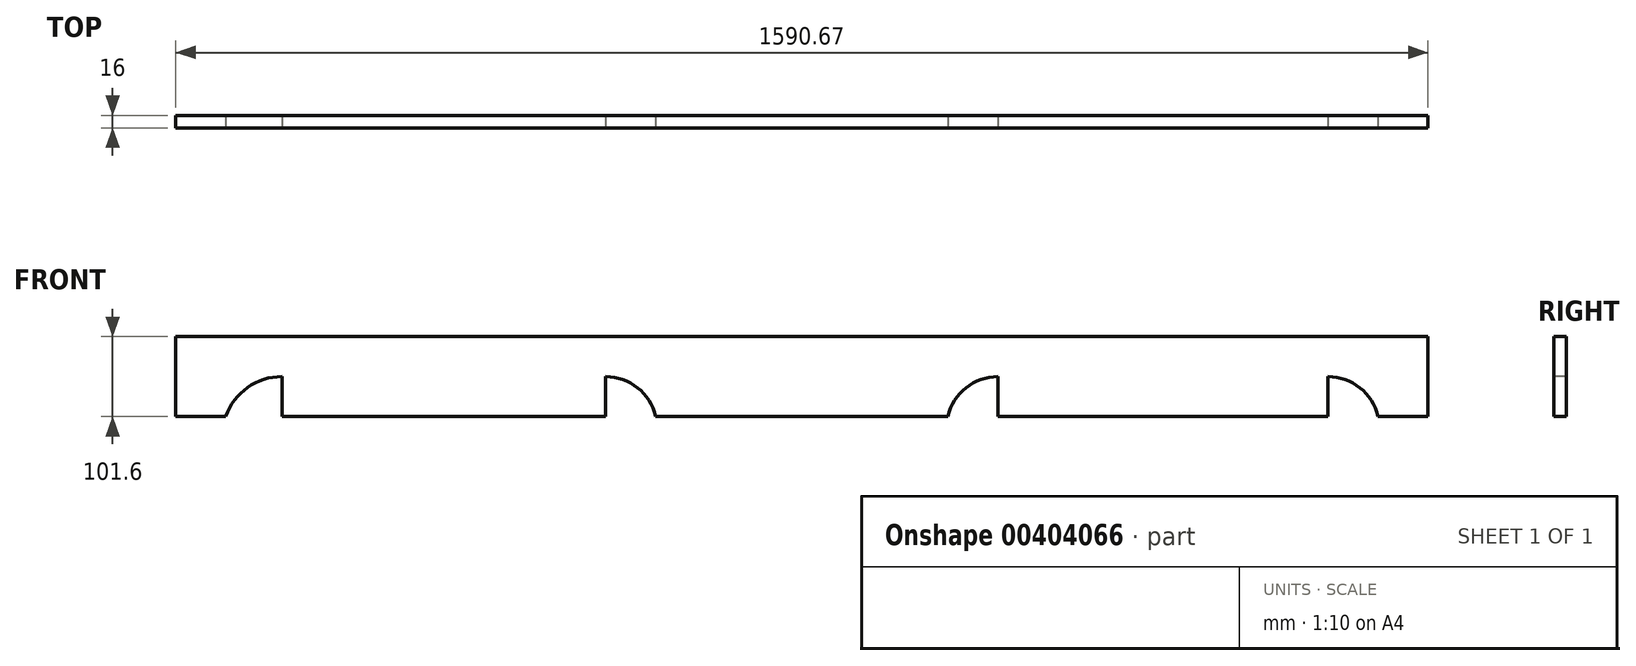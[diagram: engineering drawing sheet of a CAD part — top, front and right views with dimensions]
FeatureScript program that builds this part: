
annotation { "Feature Type Name" : "Feature", "Feature Type Description" : "" }
export const myFeature = defineFeature(function(context is Context, id is Id, definition is map)
    precondition{}
    {
        {
            var Q0;
            Q0=qCreatedBy(makeId("Front.planeOp"),FACE);
            var sketch = newSketch(context, id + "F0", { "sketchPlane" : qUnion([Q0])});
            skLineSegment(sketch, "E0.bottom", {"start": v(-777.17, 28) * mm, "end": v(813.5, 28) * mm});
            skLineSegment(sketch, "E0.top", {"start": v(-777.17, -73.6) * mm, "end": v(813.5, -73.6) * mm});
            skLineSegment(sketch, "E0.left", {"start": v(-777.17, 28) * mm, "end": v(-777.17, -73.6) * mm});
            skLineSegment(sketch, "E0.right", {"start": v(813.5, 28) * mm, "end": v(813.5, -73.6) * mm});
            skSolve(sketch);
        }
        {
            var Q0;
            Q0 = qSketchRegion(id + "F0", true);
            extrude(context, id + "F1", {"entities" : qUnion([Q0]), "depth" : 16 * mm});
        }
        {
            var Q0;
            Q0=makeQuery(id+"F1.opExtrude","CAP_FACE",FACE,{"disambiguationData":[OSD([sQuery(id+"F0.wireOp",EDGE,"E0.bottom"),sQuery(id+"F0.wireOp",EDGE,"E0.top"),sQuery(id+"F0.wireOp",EDGE,"E0.left"),sQuery(id+"F0.wireOp",EDGE,"E0.right")])],"isStart":false});
            var sketch = newSketch(context, id + "F2", { "sketchPlane" : qUnion([Q0])});
            skLineSegment(sketch, "E1.bottom", {"start": v(-167.57, 28) * mm, "end": v(203.9, 28) * mm});
            skLineSegment(sketch, "E1.top", {"start": v(-167.57, -73.6) * mm, "end": v(203.9, -73.6) * mm});
            skLineSegment(sketch, "E1.left", {"start": v(-167.57, 28) * mm, "end": v(-167.57, -73.6) * mm});
            skLineSegment(sketch, "E1.right", {"start": v(203.9, 28) * mm, "end": v(203.9, -73.6) * mm});
            skLineSegment(sketch, "E2.bottom", {"start": v(-777.17, -73.6) * mm, "end": v(-167.57, -73.6) * mm});
            skLineSegment(sketch, "E2.top", {"start": v(-777.17, -22.8) * mm, "end": v(-167.57, -22.8) * mm});
            skLineSegment(sketch, "E2.left", {"start": v(-777.17, -73.6) * mm, "end": v(-777.17, -22.8) * mm});
            skLineSegment(sketch, "E2.right", {"start": v(-167.57, -73.6) * mm, "end": v(-167.57, -22.8) * mm});
            skLineSegment(sketch, "E3.bottom", {"start": v(203.9, -73.6) * mm, "end": v(813.5, -73.6) * mm});
            skLineSegment(sketch, "E3.top", {"start": v(203.9, -22.8) * mm, "end": v(813.5, -22.8) * mm});
            skLineSegment(sketch, "E3.left", {"start": v(203.9, -73.6) * mm, "end": v(203.9, -22.8) * mm});
            skLineSegment(sketch, "E3.right", {"start": v(813.5, -73.6) * mm, "end": v(813.5, -22.8) * mm});
            skLineSegment(sketch, "E4.bottom", {"start": v(-777.17, -22.8) * mm, "end": v(-713.67, -22.8) * mm});
            skLineSegment(sketch, "E4.top", {"start": v(-777.17, -73.6) * mm, "end": v(-713.67, -73.6) * mm});
            skLineSegment(sketch, "E4.left", {"start": v(-777.17, -22.8) * mm, "end": v(-777.17, -73.6) * mm});
            skLineSegment(sketch, "E4.right", {"start": v(-713.67, -22.8) * mm, "end": v(-713.67, -73.6) * mm});
            skLineSegment(sketch, "E5.bottom", {"start": v(-167.57, -73.6) * mm, "end": v(-231.07, -73.6) * mm});
            skLineSegment(sketch, "E5.top", {"start": v(-167.57, -22.8) * mm, "end": v(-231.07, -22.8) * mm});
            skLineSegment(sketch, "E5.right", {"start": v(-231.07, -73.6) * mm, "end": v(-231.07, -22.8) * mm});
            skLineSegment(sketch, "E6.bottom", {"start": v(203.9, -73.6) * mm, "end": v(267.4, -73.6) * mm});
            skLineSegment(sketch, "E6.top", {"start": v(203.9, -22.8) * mm, "end": v(267.4, -22.8) * mm});
            skLineSegment(sketch, "E6.right", {"start": v(267.4, -73.6) * mm, "end": v(267.4, -22.8) * mm});
            skLineSegment(sketch, "E7.bottom", {"start": v(813.5, -73.6) * mm, "end": v(750, -73.6) * mm});
            skLineSegment(sketch, "E7.top", {"start": v(813.5, -22.8) * mm, "end": v(750, -22.8) * mm});
            skLineSegment(sketch, "E7.right", {"start": v(750, -73.6) * mm, "end": v(750, -22.8) * mm});
            skLineSegment(sketch, "E8.bottom", {"start": v(-713.67, -22.8) * mm, "end": v(-642.03, -22.8) * mm});
            skLineSegment(sketch, "E8.top", {"start": v(-713.67, -73.6) * mm, "end": v(-642.03, -73.6) * mm});
            skLineSegment(sketch, "E8.right", {"start": v(-642.03, -22.8) * mm, "end": v(-642.03, -73.6) * mm});
            skLineSegment(sketch, "E9.bottom", {"start": v(750, -73.6) * mm, "end": v(686.5, -73.6) * mm});
            skLineSegment(sketch, "E9.top", {"start": v(750, -22.8) * mm, "end": v(686.5, -22.8) * mm});
            skLineSegment(sketch, "E9.right", {"start": v(686.5, -73.6) * mm, "end": v(686.5, -22.8) * mm});
            skArc(sketch, "E10", {"start": v(267.4, -22.8) * mm, "mid": v(226.74, -37.07) * mm, "end": v(203.9, -73.6) * mm});
            skArc(sketch, "E11", {"start": v(750, -73.6) * mm, "mid": v(727.16, -37.07) * mm, "end": v(686.5, -22.8) * mm});
            skArc(sketch, "E12", {"start": v(-642.03, -22.8) * mm, "mid": v(-685.95, -36.8) * mm, "end": v(-713.67, -73.6) * mm});
            skArc(sketch, "E13", {"start": v(-167.57, -73.6) * mm, "mid": v(-190.41, -37.07) * mm, "end": v(-231.07, -22.8) * mm});
            skSolve(sketch);
        }
        {
            var Q0;
            Q0=makeQuery(id+"F2.imprint","IMPRINT",FACE,{"disambiguationData":[TD([[makeQuery(id+"F2.imprint","IMPRINT",EDGE,{"derivedFrom":sQuery(id+"F2.wireOp",EDGE,"E8.top")}),1.0]])]});
            var Q1;
            Q1=makeQuery(id+"F2.imprint","IMPRINT",FACE,{"disambiguationData":[TD([[makeQuery(id+"F2.imprint","IMPRINT",EDGE,{"derivedFrom":sQuery(id+"F2.wireOp",EDGE,"E2.bottom")}),1.0]])]});
            var Q2;
            Q2=makeQuery(id+"F2.imprint","IMPRINT",FACE,{"disambiguationData":[TD([[makeQuery(id+"F2.imprint","IMPRINT",EDGE,{"derivedFrom":sQuery(id+"F2.wireOp",EDGE,"E5.bottom")}),1.0]])]});
            var Q3;
            Q3=makeQuery(id+"F2.imprint","IMPRINT",FACE,{"disambiguationData":[TD([[makeQuery(id+"F2.imprint","IMPRINT",EDGE,{"derivedFrom":sQuery(id+"F2.wireOp",EDGE,"E6.bottom")}),1.0]])]});
            var Q4;
            Q4=makeQuery(id+"F2.imprint","IMPRINT",FACE,{"disambiguationData":[TD([[makeQuery(id+"F2.imprint","IMPRINT",EDGE,{"derivedFrom":sQuery(id+"F2.wireOp",EDGE,"E3.bottom")}),1.0]])]});
            var Q5;
            Q5=makeQuery(id+"F2.imprint","IMPRINT",FACE,{"disambiguationData":[TD([[makeQuery(id+"F2.imprint","IMPRINT",EDGE,{"derivedFrom":sQuery(id+"F2.wireOp",EDGE,"E9.bottom")}),1.0]])]});
            extrude(context, id + "F3", {"entities" : qUnion([Q0, Q1, Q2, Q3, Q4, Q5]), "operationType" : NewBodyOperationType.REMOVE, "oppositeDirection" : true, "depth" : 25.4 * mm});
        }
    });
